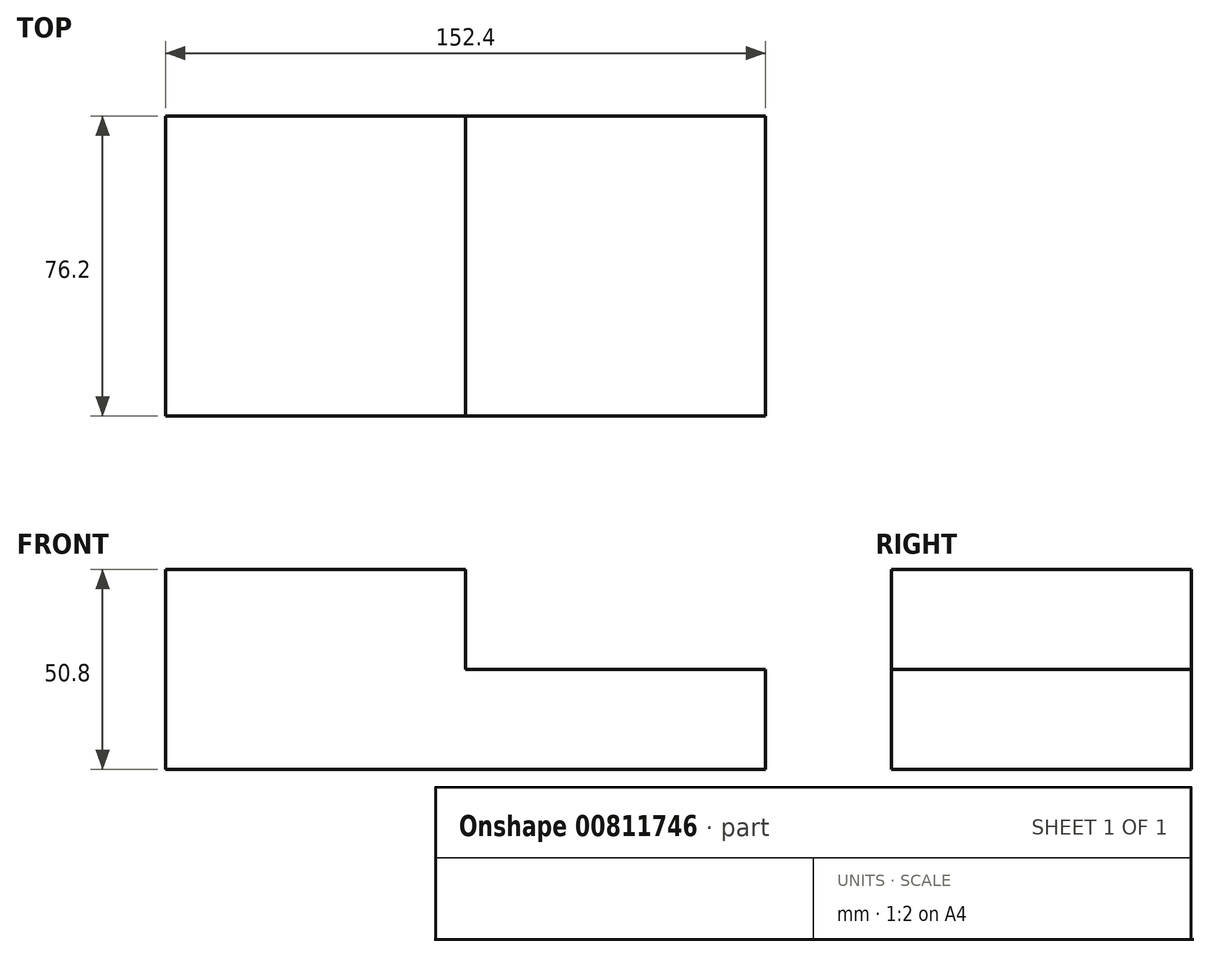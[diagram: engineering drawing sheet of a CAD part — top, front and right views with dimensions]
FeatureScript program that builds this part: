
annotation { "Feature Type Name" : "Feature", "Feature Type Description" : "" }
export const myFeature = defineFeature(function(context is Context, id is Id, definition is map)
    precondition{}
    {
        {
            var Q0;
            Q0=qCreatedBy(makeId("Front.planeOp"),FACE);
            var sketch = newSketch(context, id + "F0", { "sketchPlane" : qUnion([Q0])});
            skLineSegment(sketch, "E0", {"start": v(-76.14, 0) * mm, "end": v(-76.14, 50.8) * mm});
            skLineSegment(sketch, "E1", {"start": v(-76.14, 50.8) * mm, "end": v(0.06, 50.8) * mm});
            skLineSegment(sketch, "E2", {"start": v(0.06, 50.8) * mm, "end": v(0.06, 25.4) * mm});
            skLineSegment(sketch, "E3", {"start": v(0.06, 25.4) * mm, "end": v(76.26, 25.4) * mm});
            skLineSegment(sketch, "E4", {"start": v(76.26, 25.4) * mm, "end": v(76.26, 0) * mm});
            skLineSegment(sketch, "E5", {"start": v(76.26, 0) * mm, "end": v(-76.14, 0) * mm});
            skSolve(sketch);
        }
        {
            var Q0;
            Q0 = qSketchRegion(id + "F0", true);
            extrude(context, id + "F1", {"entities" : qUnion([Q0]), "depth" : 76.2 * mm, "offsetDistance" : 25.4 * mm});
        }
    });
